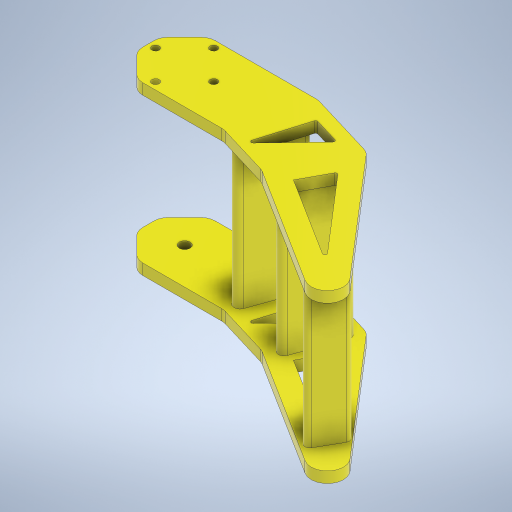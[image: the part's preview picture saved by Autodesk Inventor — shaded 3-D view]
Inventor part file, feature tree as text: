
AUTODESK INVENTOR PART (.ipt)
format: ipt  version: 2024 (Build 280153000, 153)  size: 446,976 bytes
history: native  units: in
note: dims shown in document units (in); Inventor stores cm internally (conversion verified against a paired STEP export)
features: extrude x4, sketch x3
ambient origin geometry x8: Origin, YZ Plane, XZ Plane, XY Plane, X Axis, Y Axis, Z Axis, Center Point
bodies: Solid1 (feature_tree)
feature tree (7):
  sketch  "Sketch1"  dims[d0=1.5748in d1=0.7874in]
  extrude  "Extrusion1"  Depth=0.7874in
  extrude  "Extrusion7"  Depth=0.1181in
  extrude  "Extrusion8"  Depth=0.063in
  extrude  "Extrusion9"  Depth=0.063in
  sketch  "Sketch8"  dims[d6=0.1181in d7=0.0in d32=0.315in]
  sketch  "Sketch10"  dims[d33=0.315in d34=0.315in d35=0.315in d43=0.0472in d46=0.1575in d47=0.0787in d48=0.315in d49=0.1181in d50=0.2756in d51=1.7069in d52=0.2241in d53=0.1575in d54=0.3937in d55=0.0807in d56=0.315in d57=1.5748in d59=360.0deg d64=0.1181in d69=0.1181in d70=0.1772in d71=0.4921in d72=1.5748in d73=0.0in d74=0.1181in d75=0.0in d79=0.0197in d80=0.315in d81=0.1969in d82=0.1969in d83=0.0197in d84=0.3937in d85=0.1181in d86=0.1181in d87=0.0in d88=0.063in]
